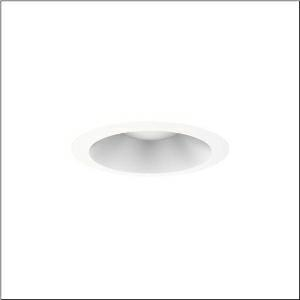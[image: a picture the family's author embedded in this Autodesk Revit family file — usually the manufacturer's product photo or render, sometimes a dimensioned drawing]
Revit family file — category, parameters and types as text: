
# Revit family: lunis_31-xl_51dn16mg42b
name_source: partatom
category: Lighting Fixtures
units: mm (PartAtom-declared; Revit-internal decimal feet)

## family parameters
Cut with Voids When Loaded = No
Host = Face
Light Source = No
Part Type = Normal
Room Calculation Point = No
Round Connector Dimension = Use Diameter
Shared = No

## types (1)
- --- (1 x LED, 2550 lm, 17 W, 4000K)
    Apparent Load = 17 VA
    CIE Flux Codes = 64 93 99 100 100
    Color Rendering = 80
    Color Temperature = 4000K
    Default Elevation = 1800 mm
    Description = Lunis 31-XL, downlight, light control with reflector, light emission: direct distribution, LED rated luminous flux: 2.550lm, light colour: 840, mains connection: 220..240V, AC/DC, 0/50..60Hz, housing, of aluminium, white, protection rating (complete): IP20, protection rating (on room side): IP54, insulation class (complete): insulation class II (safety insulation), certification: CE, ENEC, packaging unit: 1 piece
    Height = 0 mm  [stored 0 ft]
    Lamp = 1 x LED
    Lamp Light Flux = 2550 lm
    Lamp Power = 17 W
    Lamp count = 1
    Length = 259 mm
    Luminous efficacy = 150 lm/W
    Manufacturer = Siteco
    ModVariant = No
    Model = 51DN16MG42B
    Mounting Place = Ceiling
    Mounting Type = Recessed
    Number of Poles = 1
    OnlyDefault = Yes
    Power Factor = 1
    Product Name = Lunis 31-XL
    Product group = downlight
    ProductGroupID = 401
    Protection Class = Protection class II
    Protection Degree = IP 20
    RLX_Detail_Level = 1
    RLX_Emergency_Light_Flux = 0 lm
    RLX_Emergency_Type = 0
    RLX_Emergency_Type_DB = No
    RlxData = <blob elided: 24405 chars, md5=83fc2bdf>
    Socket = socket
    Standby Power = 0 W
    System Light Flux = 2550 lm
    System Power = 17 W
    Type Comments = individual setting: luminous flux: 100 % | (ON | ON | ON | OFF) | 450 mA
    Type Image = l_1345915.jpg
    URL = http://relux.com
    VarID = @adj_029647
    Voltage = 0 V
    Weight = 0.00 kg
    Width = 0 mm  [stored 0 ft]

note: [stored X ft] marks values corroborated as IEEE doubles in the binary element streams (Revit-internal decimal feet)

## geometry (parser evidence)
native form markers: Blend x4, Sweep x12
no freeform markers — native parametric forms only
